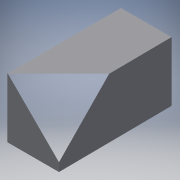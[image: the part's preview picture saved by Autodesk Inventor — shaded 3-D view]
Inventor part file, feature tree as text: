
AUTODESK INVENTOR PART (.ipt)
format: ipt  version: 2016 (Build 200138000, 138)  size: 138,752 bytes
history: native  units: mm
features: reference x5, extrude x4, sketch x4, projected_geometry x2
ambient origin geometry x8: Origin, YZ Plane, XZ Plane, XY Plane, X Axis, Y Axis, Z Axis, Center Point
bodies: Solid1 (feature_tree)
feature tree (15):
  extrude  "Extrusion1"  Depth=0.5mm
  extrude  "Extrusion2"  Depth=3.0mm
  extrude  "Extrusion3"  Depth=3.0mm TaperAngle=0.0deg
  extrude  "Extrusion4"  [1 undecoded]
  sketch  "Sketch1"  dims[d0=0.5mm d1=0.5mm]
  reference  "Reference1"
  reference  "Reference2"
  sketch  "Sketch2"  dims[d2=12.41mm d3=0.0mm d4=3.0mm]
  reference  "Reference3"
  sketch  "Sketch3"  dims[d5=12.41mm d6=0.0mm d7=3.0mm d8=0.0mm]
  reference  "Reference4"
  projected_geometry  "Projected Loop1"
  sketch  "Sketch4"  dims[d9=3.0mm d10=0.0mm]
  projected_geometry  "Projected Loop2"
  reference  "Reference5"
note: 1 required parameter value undecoded (feature->parameter linkage not recoverable at this tier; creation-order binding heuristic only, values carry confidence <= 0.55)
